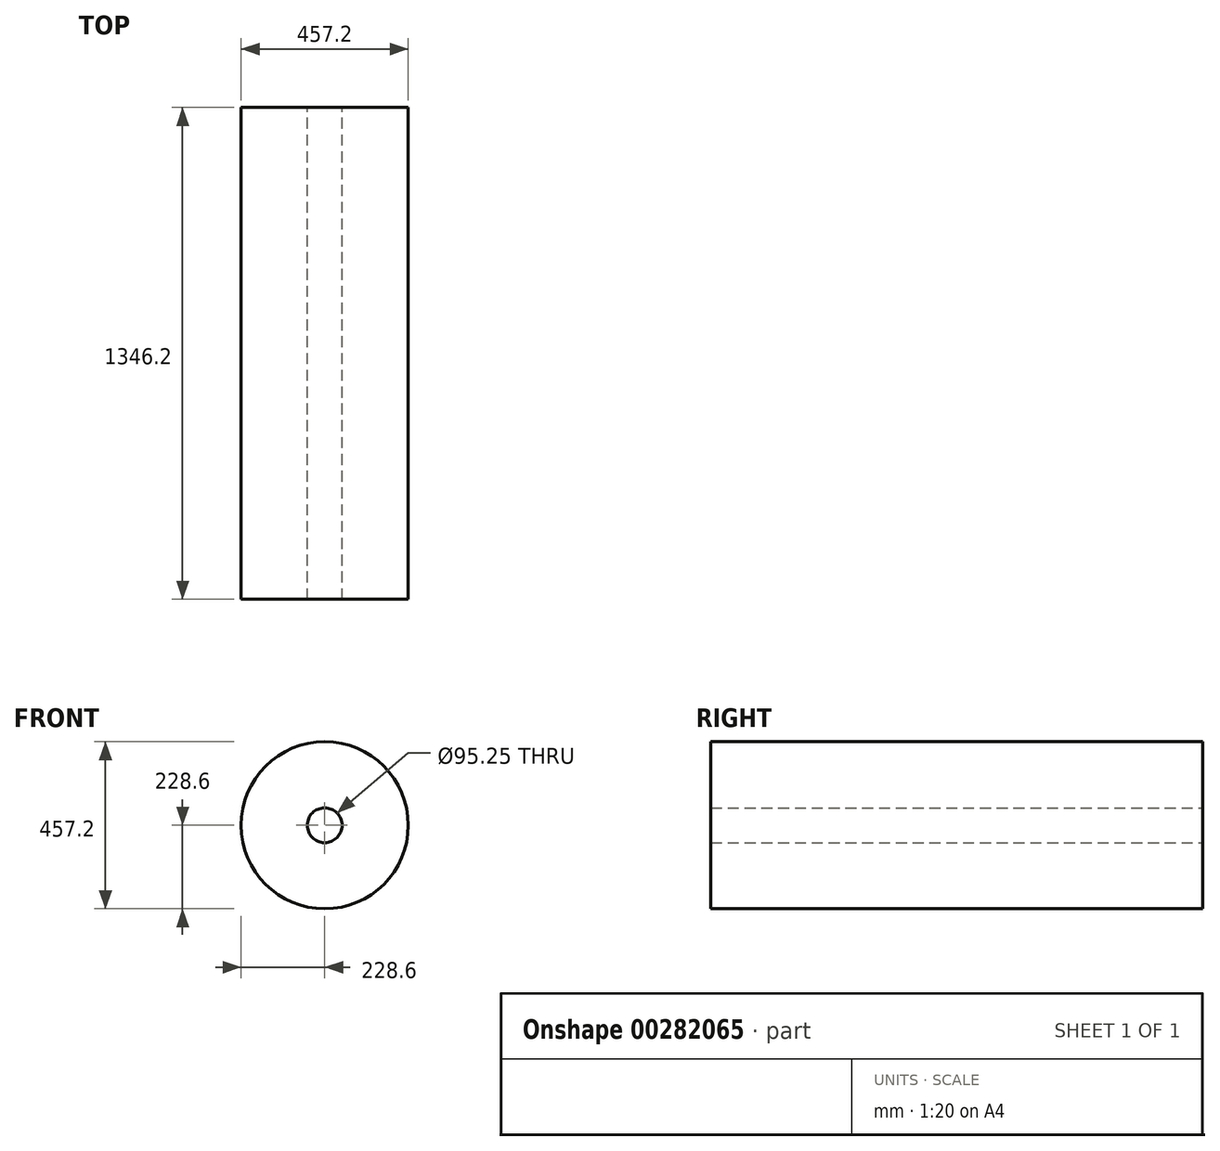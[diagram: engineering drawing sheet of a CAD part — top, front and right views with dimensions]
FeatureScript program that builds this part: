
annotation { "Feature Type Name" : "Feature", "Feature Type Description" : "" }
export const myFeature = defineFeature(function(context is Context, id is Id, definition is map)
    precondition{}
    {
        {
            var Q0;
            Q0=qCreatedBy(makeId("Front.planeOp"),FACE);
            var sketch = newSketch(context, id + "F0", { "sketchPlane" : qUnion([Q0])});
            skCircle(sketch, "E0", {"center": v(0, 0) * mm, "radius": 228.6 * mm});
            skCircle(sketch, "E1", {"center": v(0, 0) * mm, "radius": 47.63 * mm});
            skSolve(sketch);
        }
        {
            var Q0;
            Q0 = qSketchRegion(id + "F0", true);
            extrude(context, id + "F1", {"entities" : qUnion([Q0]), "depth" : 1346.2 * mm, "offsetDistance" : 25.4 * mm});
        }
    });
